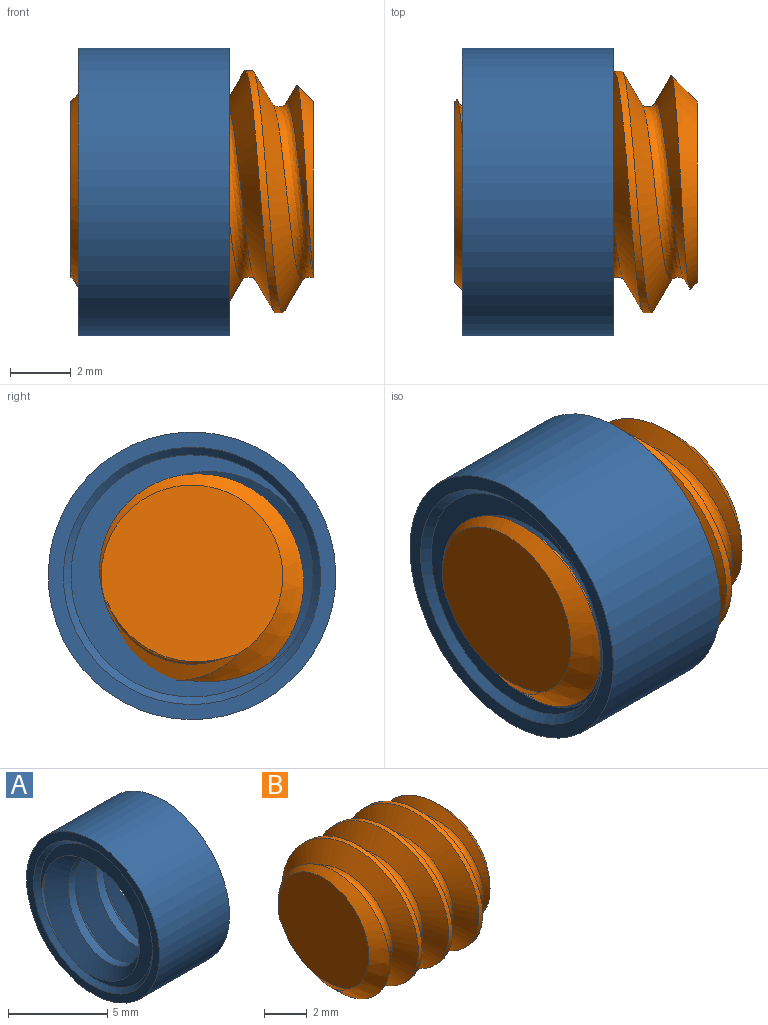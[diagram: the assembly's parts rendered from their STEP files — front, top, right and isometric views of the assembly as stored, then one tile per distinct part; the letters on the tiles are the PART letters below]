
ASSEMBLY  parts=2 mates=1
PART A: 13 faces, bbox 6.6x10.1x10 mm
  f0: cylinder r=4.75mm len=9.5mm, axis (1,0,0), area 149.2mm2, adj f1,f2
  f1: plane 9.5x9.5mm, normal (-1,0,0), area 14.1mm2, adj f0,f3
  f2: plane 9.5x9.5mm, normal (1,0,0), area 14.1mm2, adj f0,f4
  f3: cone r=4.25mm half-angle=45deg, axis (-1,0,0), area 9.2mm2, adj f1,f8,f10
  f4: cone r=4mm half-angle=45deg, axis (1,0,0), area 9.2mm2, adj f2,f9,f11
  f5: bspline ~9.43x8.17mm, area 62.7mm2, adj f7,f8,f9,f10,f11,f12
  f6: bspline ~9.43x8.17mm, area 62.7mm2, adj f7,f8,f9,f10,f11,f12
  f7: bspline ~9.64x8.35mm, area 16.9mm2, adj f5,f6,f8,f9
  f8: plane 3.02x2.97mm, normal (1,0,0), area 0.5mm2, adj f3,f5,f6,f7
  f9: plane 3.02x2.97mm, normal (-1,0,0), area 0.5mm2, adj f4,f5,f6,f7
  f10: plane 8.47x8.47mm, normal (-1,0,0), area 12.1mm2, adj f3,f5,f6,f12
  f11: plane 8.47x8.47mm, normal (1,0,0), area 12.2mm2, adj f4,f5,f6,f12
  f12: cylinder r=3mm len=6mm, axis (-1,0,0), area 21.2mm2, adj f5,f6,f10,f11
PART B: 8 faces, bbox 9.6x9.3x8.1 mm
  f0: cylinder r=4mm len=8mm, axis (-1,0,0), area 18.9mm2, adj f4,f5,f6,f7
  f1: plane 6.05x5.89mm, normal (1,0,0), area 27.5mm2, adj f3,f4,f5,f6
  f2: plane 6.05x5.89mm, normal (-1,0,0), area 27.5mm2, adj f3,f4,f5,f7
  f3: bspline ~9.5x6.74mm, area 40.1mm2, adj f1,f2,f4,f5
  f4: bspline ~9.24x8.96mm, area 95.7mm2, adj f0,f1,f2,f3,f6,f7
  f5: bspline ~9.24x8.96mm, area 95.9mm2, adj f0,f1,f2,f3,f6,f7
  f6: cone r=3mm half-angle=45deg, axis (-1,0,0), area 12.4mm2, adj f0,f1,f4,f5
  f7: cone r=4mm half-angle=45deg, axis (1,0,0), area 12.4mm2, adj f0,f2,f4,f5
PLACE A rot(axis=(-1,0,0),132.4deg) t=(7.74,0,0)mm
PLACE B at identity fixed
MATE cylindrical B.f0 <-> A.f0  axis (1,0,0) through (8,0,0)mm
